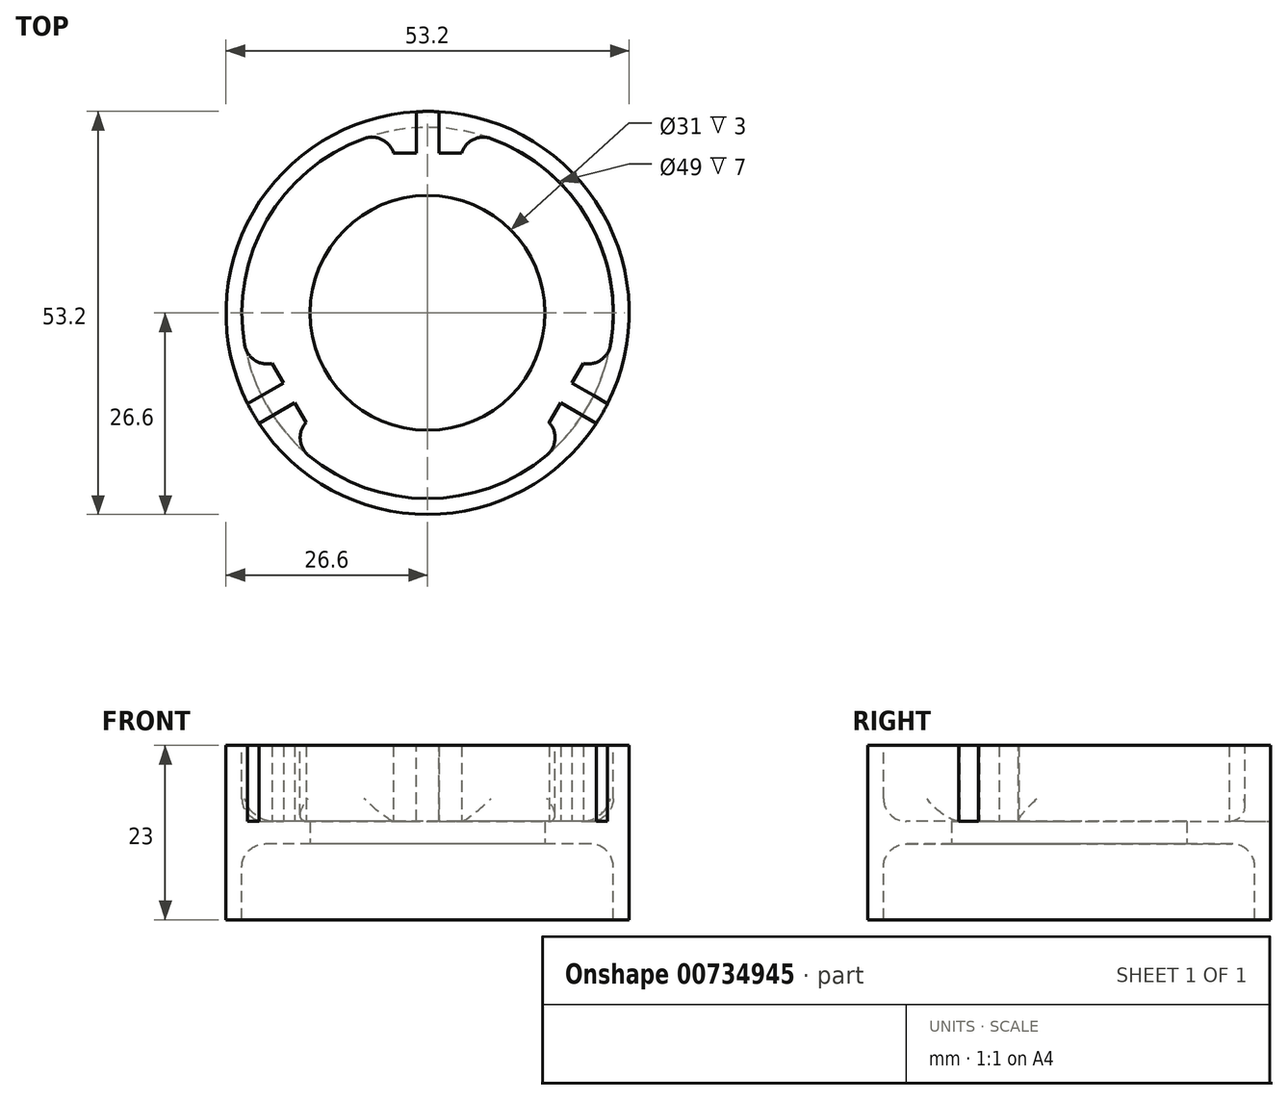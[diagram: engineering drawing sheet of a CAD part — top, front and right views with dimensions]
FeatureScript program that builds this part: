
annotation { "Feature Type Name" : "Feature", "Feature Type Description" : "" }
export const myFeature = defineFeature(function(context is Context, id is Id, definition is map)
    precondition{}
    {
        {
            var Q0;
            Q0=qCreatedBy(makeId("Top.planeOp"),FACE);
            var sketch = newSketch(context, id + "F0", { "sketchPlane" : qUnion([Q0])});
            skCircle(sketch, "E0", {"center": v(0, 0) * mm, "radius": 15.5 * mm});
            skCircle(sketch, "E1", {"center": v(0, 0) * mm, "radius": 26.6 * mm});
            skSolve(sketch);
        }
        {
            var Q0;
            Q0=makeQuery(id+"F0.imprint","IMPRINT",FACE,{"disambiguationData":[TD([[makeQuery(id+"F0.imprint","IMPRINT",EDGE,{"derivedFrom":sQuery(id+"F0.wireOp",EDGE,"E0")}),-1.0]])]});
            extrude(context, id + "F1", {"entities" : qUnion([Q0]), "depth" : 3 * mm, "offsetDistance" : 25 * mm});
        }
        {
            var Q0;
            Q0=makeQuery(id+"F1.opExtrude","CAP_FACE",FACE,{"disambiguationData":[OSD([sQuery(id+"F0.wireOp",EDGE,"E0"),sQuery(id+"F0.wireOp",EDGE,"E1")])],"isStart":false});
            var sketch = newSketch(context, id + "F2", { "sketchPlane" : qUnion([Q0])});
            skLineSegment(sketch, "E2.left", {"start": v(-1.5, 23.14) * mm, "end": v(-1.5, 26.56) * mm});
            skLineSegment(sketch, "E2.right", {"start": v(1.5, 23.14) * mm, "end": v(1.5, 26.56) * mm});
            skPoint(sketch, "E2.middle", {"position": v(0, 26.6) * mm});
            skLineSegment(sketch, "E3.bottom", {"start": v(-4.5, 21.12) * mm, "end": v(4.5, 21.12) * mm});
            skCircle(sketch, "E4", {"center": v(0, 0) * mm, "radius": 26.6 * mm});
            skPoint(sketch, "E5.orphan", {"position": v(1.5, 30.06) * mm});
            skPoint(sketch, "E3.top.end.orphan", {"position": v(4.5, 32.08) * mm});
            skPoint(sketch, "E6.orphan", {"position": v(-1.5, 30.06) * mm});
            skPoint(sketch, "E7.orphan", {"position": v(-4.5, 32.08) * mm});
            skLineSegment(sketch, "E8", {"start": v(4.5, 21.12) * mm, "end": v(4.5, 26.22) * mm});
            skLineSegment(sketch, "E9", {"start": v(-4.5, 21.12) * mm, "end": v(-4.5, 26.22) * mm});
            skLineSegment(sketch, "E10", {"start": v(1.5, 23.14) * mm, "end": v(1.5, 21.12) * mm});
            skLineSegment(sketch, "E11", {"start": v(-1.5, 23.14) * mm, "end": v(-1.5, 21.12) * mm});
            skLineSegment(sketch, "E12.1.0", {"start": v(-20.8, -10.27) * mm, "end": v(-23.75, -11.98) * mm});
            skPoint(sketch, "E12.1.1", {"position": v(-25.53, -19.94) * mm});
            skLineSegment(sketch, "E12.1.2", {"start": v(-19.3, -12.87) * mm, "end": v(-17.54, -11.86) * mm});
            skPoint(sketch, "E12.1.3", {"position": v(-26.78, -13.73) * mm});
            skLineSegment(sketch, "E12.1.4", {"start": v(-16.04, -14.46) * mm, "end": v(-20.45, -17) * mm});
            skLineSegment(sketch, "E12.1.5", {"start": v(-20.8, -10.27) * mm, "end": v(-19.04, -9.26) * mm});
            skLineSegment(sketch, "E12.1.6", {"start": v(-16.04, -14.46) * mm, "end": v(-20.54, -6.66) * mm});
            skLineSegment(sketch, "E12.1.7", {"start": v(-19.3, -12.87) * mm, "end": v(-22.25, -14.58) * mm});
            skPoint(sketch, "E12.1.8", {"position": v(-23.04, -13.3) * mm});
            skPoint(sketch, "E12.1.10", {"position": v(-25.28, -16.33) * mm});
            skLineSegment(sketch, "E12.1.11", {"start": v(-20.54, -6.66) * mm, "end": v(-24.95, -9.21) * mm});
            skPoint(sketch, "E12.1.12", {"position": v(-30.03, -12.14) * mm});
            skPoint(sketch, "E12.1.13", {"position": v(-23.04, -13.3) * mm});
            skLineSegment(sketch, "E12.2.0", {"start": v(19.3, -12.87) * mm, "end": v(22.25, -14.58) * mm});
            skPoint(sketch, "E12.2.1", {"position": v(30.03, -12.14) * mm});
            skLineSegment(sketch, "E12.2.2", {"start": v(20.8, -10.27) * mm, "end": v(19.04, -9.26) * mm});
            skPoint(sketch, "E12.2.3", {"position": v(25.28, -16.33) * mm});
            skLineSegment(sketch, "E12.2.4", {"start": v(20.54, -6.66) * mm, "end": v(24.95, -9.21) * mm});
            skLineSegment(sketch, "E12.2.5", {"start": v(19.3, -12.87) * mm, "end": v(17.54, -11.86) * mm});
            skLineSegment(sketch, "E12.2.6", {"start": v(20.54, -6.66) * mm, "end": v(16.04, -14.46) * mm});
            skLineSegment(sketch, "E12.2.7", {"start": v(20.8, -10.27) * mm, "end": v(23.75, -11.98) * mm});
            skPoint(sketch, "E12.2.8", {"position": v(23.04, -13.3) * mm});
            skPoint(sketch, "E12.2.10", {"position": v(26.78, -13.73) * mm});
            skLineSegment(sketch, "E12.2.11", {"start": v(16.04, -14.46) * mm, "end": v(20.45, -17) * mm});
            skPoint(sketch, "E12.2.12", {"position": v(25.53, -19.94) * mm});
            skPoint(sketch, "E12.2.13", {"position": v(23.04, -13.3) * mm});
            skSolve(sketch);
        }
        {
            var Q0;
            Q0=qCreatedBy(makeId("Top.planeOp"),FACE);
            var sketch = newSketch(context, id + "F3", { "sketchPlane" : qUnion([Q0])});
            skCircle(sketch, "E13", {"center": v(0, 0) * mm, "radius": 26.6 * mm});
            skCircle(sketch, "E14", {"center": v(0, 0) * mm, "radius": 24.5 * mm});
            skSolve(sketch);
        }
        {
            var Q0;
            Q0 = qSketchRegion(id + "F3", true);
            extrude(context, id + "F4", {"entities" : qUnion([Q0]), "operationType" : NewBodyOperationType.ADD, "oppositeDirection" : true, "depth" : 10 * mm, "offsetDistance" : 25 * mm, "hasSecondDirection" : true, "secondDirectionOppositeDirection" : false, "secondDirectionDepth" : 13 * mm});
        }
        {
            var Q0;
            {var subQ4=sQuery(id+"F2.wireOp",EDGE,"E2.right");Q0=makeQuery(id+"F2.imprint","IMPRINT",FACE,{"disambiguationData":[TD([[makeQuery(id+"F2.imprint","IMPRINT",EDGE,{"derivedFrom":subQ4}),-1.0]])]});}
            var Q1;
            {var subQ3=sQuery(id+"F2.wireOp",EDGE,"E2.left");Q1=makeQuery(id+"F2.imprint","IMPRINT",FACE,{"disambiguationData":[TD([[makeQuery(id+"F2.imprint","IMPRINT",EDGE,{"derivedFrom":subQ3}),1.0]])]});}
            var Q2;
            {var subQ1=sQuery(id+"F2.wireOp",EDGE,"E12.1.2");Q2=makeQuery(id+"F2.imprint","IMPRINT",FACE,{"disambiguationData":[TD([[makeQuery(id+"F2.imprint","IMPRINT",EDGE,{"derivedFrom":subQ1}),-1.0]])]});}
            var Q3;
            {var subQ3=sQuery(id+"F2.wireOp",EDGE,"E12.1.0");Q3=makeQuery(id+"F2.imprint","IMPRINT",FACE,{"disambiguationData":[TD([[makeQuery(id+"F2.imprint","IMPRINT",EDGE,{"derivedFrom":subQ3}),-1.0]])]});}
            var Q4;
            {var subQ1=sQuery(id+"F2.wireOp",EDGE,"E12.2.0");Q4=makeQuery(id+"F2.imprint","IMPRINT",FACE,{"disambiguationData":[TD([[makeQuery(id+"F2.imprint","IMPRINT",EDGE,{"derivedFrom":subQ1}),-1.0]])]});}
            var Q5;
            {var subQ1=sQuery(id+"F2.wireOp",EDGE,"E12.2.2");Q5=makeQuery(id+"F2.imprint","IMPRINT",FACE,{"disambiguationData":[TD([[makeQuery(id+"F2.imprint","IMPRINT",EDGE,{"derivedFrom":subQ1}),-1.0]])]});}
            extrude(context, id + "F5", {"entities" : qUnion([Q0, Q1, Q2, Q3, Q4, Q5]), "operationType" : NewBodyOperationType.ADD, "depth" : 10 * mm, "offsetDistance" : 25 * mm});
        }
        {
            var Q0;
            {var subQ0=sQuery(id+"F2.wireOp",EDGE,"E4");var subQ1=sQuery(id+"F2.wireOp",EDGE,"E12.2.6");var subQ2=sQuery(id+"F2.wireOp",EDGE,"E12.1.6");var subQ3=sQuery(id+"F2.wireOp",EDGE,"E3.bottom");Q0=makeQuery(id+"F5.boolean.opBoolean","MERGE",FACE,{"derivedFrom":[makeQuery(id+"F4.opExtrude","CAP_FACE",FACE,{"disambiguationData":[OSD([sQuery(id+"F3.wireOp",EDGE,"E13"),sQuery(id+"F3.wireOp",EDGE,"E14")])],"isStart":true}),makeQuery(id+"F5.opExtrude","CAP_FACE",FACE,{"disambiguationData":[OSD([sQuery(id+"F2.wireOp",EDGE,"E2.left"),subQ3,sQuery(id+"F2.wireOp",EDGE,"E9"),sQuery(id+"F2.wireOp",EDGE,"E11"),subQ0])],"isStart":false}),makeQuery(id+"F5.opExtrude","CAP_FACE",FACE,{"disambiguationData":[OSD([sQuery(id+"F2.wireOp",EDGE,"E2.right"),subQ3,sQuery(id+"F2.wireOp",EDGE,"E8"),sQuery(id+"F2.wireOp",EDGE,"E10"),subQ0])],"isStart":false}),makeQuery(id+"F5.opExtrude","CAP_FACE",FACE,{"disambiguationData":[OSD([sQuery(id+"F2.wireOp",EDGE,"E12.1.0"),sQuery(id+"F2.wireOp",EDGE,"E12.1.5"),subQ2,sQuery(id+"F2.wireOp",EDGE,"E12.1.11"),subQ0])],"isStart":false}),makeQuery(id+"F5.opExtrude","CAP_FACE",FACE,{"disambiguationData":[OSD([sQuery(id+"F2.wireOp",EDGE,"E12.1.2"),sQuery(id+"F2.wireOp",EDGE,"E12.1.4"),subQ2,sQuery(id+"F2.wireOp",EDGE,"E12.1.7"),subQ0])],"isStart":false}),makeQuery(id+"F5.opExtrude","CAP_FACE",FACE,{"disambiguationData":[OSD([sQuery(id+"F2.wireOp",EDGE,"E12.2.0"),sQuery(id+"F2.wireOp",EDGE,"E12.2.5"),subQ1,subQ0,sQuery(id+"F2.wireOp",EDGE,"E12.2.11")])],"isStart":false}),makeQuery(id+"F5.opExtrude","CAP_FACE",FACE,{"disambiguationData":[OSD([sQuery(id+"F2.wireOp",EDGE,"E12.2.2"),sQuery(id+"F2.wireOp",EDGE,"E12.2.4"),subQ1,sQuery(id+"F2.wireOp",EDGE,"E12.2.7"),subQ0])],"isStart":false})]});}
            var sketch = newSketch(context, id + "F6", { "sketchPlane" : qUnion([Q0])});
            skLineSegment(sketch, "E15", {"start": v(-1.5, 21.12) * mm, "end": v(-1.5, 26.56) * mm});
            skLineSegment(sketch, "E16", {"start": v(1.5, 21.12) * mm, "end": v(1.5, 26.56) * mm});
            skLineSegment(sketch, "E17", {"start": v(19.04, -9.26) * mm, "end": v(23.75, -11.98) * mm});
            skLineSegment(sketch, "E18", {"start": v(17.54, -11.86) * mm, "end": v(22.25, -14.58) * mm});
            skLineSegment(sketch, "E19", {"start": v(-19.04, -9.26) * mm, "end": v(-23.75, -11.98) * mm});
            skLineSegment(sketch, "E20", {"start": v(-17.54, -11.86) * mm, "end": v(-22.25, -14.58) * mm});
            skSolve(sketch);
        }
        {
            var Q0;
            {var subQ2=sQuery(id+"F6.wireOp",EDGE,"E20");Q0=makeQuery(id+"F6.imprint","IMPRINT",FACE,{"disambiguationData":[TD([[makeQuery(id+"F6.imprint","IMPRINT",EDGE,{"derivedFrom":subQ2}),-1.0]])]});}
            var Q1;
            {var subQ0=sQuery(id+"F2.wireOp",EDGE,"E12.2.0");var subQ1=makeQuery(id+"F5.opExtrude","CAP_EDGE",EDGE,{"disambiguationData":[OSD([subQ0])],"isStart":false});Q1=makeQuery(id+"F6.imprint","IMPRINT",FACE,{"disambiguationData":[TD([[makeQuery(id+"F6.imprint","IMPRINT",EDGE,{"derivedFrom":subQ1}),-1.0]])]});}
            var Q2;
            {var subQ5=sQuery(id+"F3.wireOp",EDGE,"E13");var subQ11=sQuery(id+"F6.wireOp",EDGE,"E16");var subQ14=makeQuery(id+"F4.opExtrude","CAP_EDGE",EDGE,{"disambiguationData":[OSD([subQ5])],"isStart":true});var subQ16=makeQuery(id+"F6.imprint","INTERSECT",VERTEX,{"derivedFrom":[subQ14,subQ11]});Q2=makeQuery(id+"F6.imprint","IMPRINT",FACE,{"disambiguationData":[TD([[makeQuery(id+"F6.imprint","IMPRINT",EDGE,{"disambiguationData":[TD([[subQ16,1.0]])],"derivedFrom":subQ11}),1.0]])]});}
            extrude(context, id + "F7", {"entities" : qUnion([Q0, Q1, Q2]), "operationType" : NewBodyOperationType.REMOVE, "oppositeDirection" : true, "depth" : 10 * mm, "offsetDistance" : 25 * mm});
        }
        {
            var Q0;
            {var subQ0=makeQuery(id+"F1.opExtrude","CAP_FACE",FACE,{"disambiguationData":[OSD([sQuery(id+"F0.wireOp",EDGE,"E0"),sQuery(id+"F0.wireOp",EDGE,"E1")])],"isStart":false});var subQ1=makeQuery(id+"F4.opExtrude","SWEPT_FACE",FACE,{"disambiguationData":[OSD([sQuery(id+"F3.wireOp",EDGE,"E14")])]});Q0=makeQuery(id+"F5.boolean.opBoolean","SPLIT",EDGE,{"disambiguationData":[TD([makeQuery(id+"F5.opExtrude","SWEPT_FACE",FACE,{"disambiguationData":[OSD([sQuery(id+"F2.wireOp",EDGE,"E8")])]})])],"derivedFrom":makeQuery(id+"F4.boolean.opBoolean","INTERSECT",EDGE,{"derivedFrom":[subQ0,subQ1]})});}
            var Q1;
            {var subQ0=makeQuery(id+"F1.opExtrude","CAP_FACE",FACE,{"disambiguationData":[OSD([sQuery(id+"F0.wireOp",EDGE,"E0"),sQuery(id+"F0.wireOp",EDGE,"E1")])],"isStart":false});var subQ1=makeQuery(id+"F4.opExtrude","SWEPT_FACE",FACE,{"disambiguationData":[OSD([sQuery(id+"F3.wireOp",EDGE,"E14")])]});Q1=makeQuery(id+"F5.boolean.opBoolean","SPLIT",EDGE,{"disambiguationData":[TD([makeQuery(id+"F5.opExtrude","SWEPT_FACE",FACE,{"disambiguationData":[OSD([sQuery(id+"F2.wireOp",EDGE,"E9")])]})])],"derivedFrom":makeQuery(id+"F4.boolean.opBoolean","INTERSECT",EDGE,{"derivedFrom":[subQ0,subQ1]})});}
            var Q2;
            {var subQ0=makeQuery(id+"F1.opExtrude","CAP_FACE",FACE,{"disambiguationData":[OSD([sQuery(id+"F0.wireOp",EDGE,"E0"),sQuery(id+"F0.wireOp",EDGE,"E1")])],"isStart":false});var subQ1=makeQuery(id+"F4.opExtrude","SWEPT_FACE",FACE,{"disambiguationData":[OSD([sQuery(id+"F3.wireOp",EDGE,"E14")])]});Q2=makeQuery(id+"F5.boolean.opBoolean","SPLIT",EDGE,{"disambiguationData":[TD([makeQuery(id+"F5.opExtrude","SWEPT_FACE",FACE,{"disambiguationData":[OSD([sQuery(id+"F2.wireOp",EDGE,"E12.1.4")])]})])],"derivedFrom":makeQuery(id+"F4.boolean.opBoolean","INTERSECT",EDGE,{"derivedFrom":[subQ0,subQ1]})});}
            var Q3;
            Q3=makeQuery(id+"F4.boolean.opBoolean","INTERSECT",EDGE,{"derivedFrom":[makeQuery(id+"F1.opExtrude","CAP_FACE",FACE,{"disambiguationData":[OSD([sQuery(id+"F0.wireOp",EDGE,"E0"),sQuery(id+"F0.wireOp",EDGE,"E1")])],"isStart":true}),makeQuery(id+"F4.opExtrude","SWEPT_FACE",FACE,{"disambiguationData":[OSD([sQuery(id+"F3.wireOp",EDGE,"E14")])]})]});
            var Q4;
            {var subQ0=sQuery(id+"F3.wireOp",EDGE,"E14");Q4=makeQuery(id+"F5.boolean.opBoolean","INTERSECT",EDGE,{"derivedFrom":[makeQuery(id+"F4.boolean.opBoolean","SPLIT",FACE,{"disambiguationData":[TD([makeQuery(id+"F1.opExtrude","CAP_FACE",FACE,{"disambiguationData":[OSD([sQuery(id+"F0.wireOp",EDGE,"E0"),sQuery(id+"F0.wireOp",EDGE,"E1")])],"isStart":false})])],"derivedFrom":makeQuery(id+"F4.opExtrude","SWEPT_FACE",FACE,{"disambiguationData":[OSD([subQ0])]})}),makeQuery(id+"F5.opExtrude","SWEPT_FACE",FACE,{"disambiguationData":[OSD([sQuery(id+"F2.wireOp",EDGE,"E12.2.4")])]})]});}
            var Q5;
            {var subQ0=sQuery(id+"F3.wireOp",EDGE,"E14");Q5=makeQuery(id+"F5.boolean.opBoolean","INTERSECT",EDGE,{"derivedFrom":[makeQuery(id+"F4.boolean.opBoolean","SPLIT",FACE,{"disambiguationData":[TD([makeQuery(id+"F1.opExtrude","CAP_FACE",FACE,{"disambiguationData":[OSD([sQuery(id+"F0.wireOp",EDGE,"E0"),sQuery(id+"F0.wireOp",EDGE,"E1")])],"isStart":false})])],"derivedFrom":makeQuery(id+"F4.opExtrude","SWEPT_FACE",FACE,{"disambiguationData":[OSD([subQ0])]})}),makeQuery(id+"F5.opExtrude","SWEPT_FACE",FACE,{"disambiguationData":[OSD([sQuery(id+"F2.wireOp",EDGE,"E12.2.11")])]})]});}
            var Q6;
            {var subQ0=sQuery(id+"F3.wireOp",EDGE,"E14");Q6=makeQuery(id+"F5.boolean.opBoolean","INTERSECT",EDGE,{"derivedFrom":[makeQuery(id+"F4.boolean.opBoolean","SPLIT",FACE,{"disambiguationData":[TD([makeQuery(id+"F1.opExtrude","CAP_FACE",FACE,{"disambiguationData":[OSD([sQuery(id+"F0.wireOp",EDGE,"E0"),sQuery(id+"F0.wireOp",EDGE,"E1")])],"isStart":false})])],"derivedFrom":makeQuery(id+"F4.opExtrude","SWEPT_FACE",FACE,{"disambiguationData":[OSD([subQ0])]})}),makeQuery(id+"F5.opExtrude","SWEPT_FACE",FACE,{"disambiguationData":[OSD([sQuery(id+"F2.wireOp",EDGE,"E9")])]})]});}
            var Q7;
            {var subQ0=sQuery(id+"F3.wireOp",EDGE,"E14");Q7=makeQuery(id+"F5.boolean.opBoolean","INTERSECT",EDGE,{"derivedFrom":[makeQuery(id+"F4.boolean.opBoolean","SPLIT",FACE,{"disambiguationData":[TD([makeQuery(id+"F1.opExtrude","CAP_FACE",FACE,{"disambiguationData":[OSD([sQuery(id+"F0.wireOp",EDGE,"E0"),sQuery(id+"F0.wireOp",EDGE,"E1")])],"isStart":false})])],"derivedFrom":makeQuery(id+"F4.opExtrude","SWEPT_FACE",FACE,{"disambiguationData":[OSD([subQ0])]})}),makeQuery(id+"F5.opExtrude","SWEPT_FACE",FACE,{"disambiguationData":[OSD([sQuery(id+"F2.wireOp",EDGE,"E8")])]})]});}
            var Q8;
            {var subQ0=sQuery(id+"F3.wireOp",EDGE,"E14");Q8=makeQuery(id+"F5.boolean.opBoolean","INTERSECT",EDGE,{"derivedFrom":[makeQuery(id+"F4.boolean.opBoolean","SPLIT",FACE,{"disambiguationData":[TD([makeQuery(id+"F1.opExtrude","CAP_FACE",FACE,{"disambiguationData":[OSD([sQuery(id+"F0.wireOp",EDGE,"E0"),sQuery(id+"F0.wireOp",EDGE,"E1")])],"isStart":false})])],"derivedFrom":makeQuery(id+"F4.opExtrude","SWEPT_FACE",FACE,{"disambiguationData":[OSD([subQ0])]})}),makeQuery(id+"F5.opExtrude","SWEPT_FACE",FACE,{"disambiguationData":[OSD([sQuery(id+"F2.wireOp",EDGE,"E12.1.4")])]})]});}
            var Q9;
            {var subQ0=sQuery(id+"F3.wireOp",EDGE,"E14");Q9=makeQuery(id+"F5.boolean.opBoolean","INTERSECT",EDGE,{"derivedFrom":[makeQuery(id+"F4.boolean.opBoolean","SPLIT",FACE,{"disambiguationData":[TD([makeQuery(id+"F1.opExtrude","CAP_FACE",FACE,{"disambiguationData":[OSD([sQuery(id+"F0.wireOp",EDGE,"E0"),sQuery(id+"F0.wireOp",EDGE,"E1")])],"isStart":false})])],"derivedFrom":makeQuery(id+"F4.opExtrude","SWEPT_FACE",FACE,{"disambiguationData":[OSD([subQ0])]})}),makeQuery(id+"F5.opExtrude","SWEPT_FACE",FACE,{"disambiguationData":[OSD([sQuery(id+"F2.wireOp",EDGE,"E12.1.11")])]})]});}
            fillet(context, id + "F8", {"entities" : qUnion([Q0, Q1, Q2, Q3, Q4, Q5, Q6, Q7, Q8, Q9]), "radius" : 3 * mm, "tangentPropagation" : true, "allowEdgeOverflow" : false});
        }
    });
